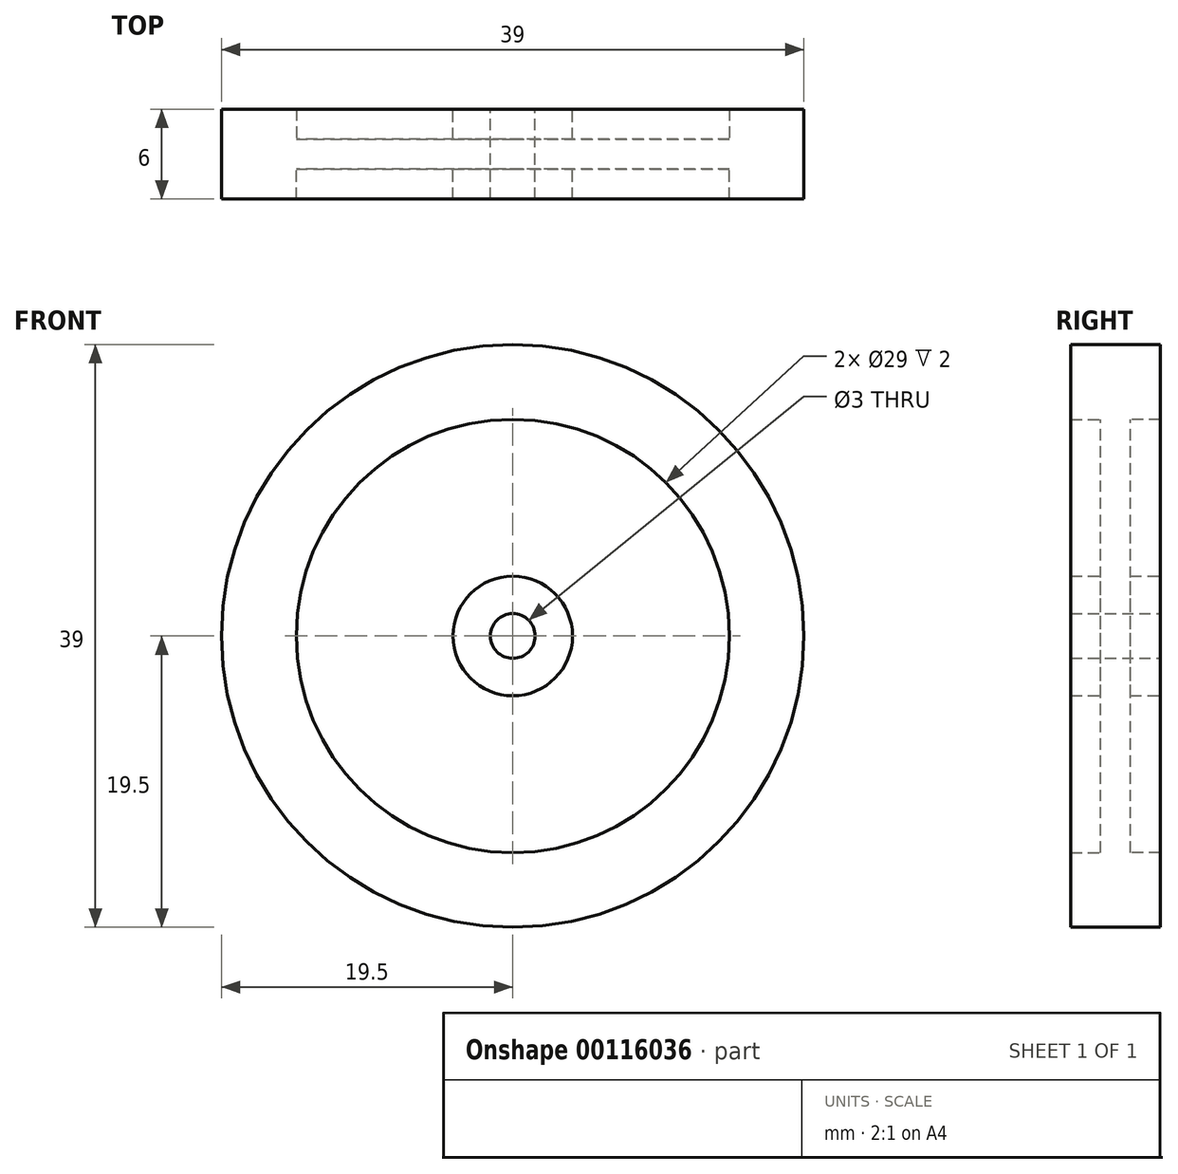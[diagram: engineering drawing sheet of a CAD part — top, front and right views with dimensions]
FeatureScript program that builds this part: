
annotation { "Feature Type Name" : "Feature", "Feature Type Description" : "" }
export const myFeature = defineFeature(function(context is Context, id is Id, definition is map)
    precondition{}
    {
        {
            var Q0;
            Q0=qCreatedBy(makeId("Front.planeOp"),FACE);
            var sketch = newSketch(context, id + "F0", { "sketchPlane" : qUnion([Q0])});
            skCircle(sketch, "E0", {"center": v(0, 0) * mm, "radius": 14.5 * mm});
            skCircle(sketch, "E1", {"center": v(0, 0) * mm, "radius": 4 * mm});
            skCircle(sketch, "E2", {"center": v(0, 0) * mm, "radius": 19.5 * mm});
            skCircle(sketch, "E3", {"center": v(0, 0) * mm, "radius": 1.5 * mm});
            skSolve(sketch);
        }
        {
            var Q0;
            Q0=makeQuery(id+"F0.imprint","IMPRINT",FACE,{"disambiguationData":[TD([[makeQuery(id+"F0.imprint","IMPRINT",EDGE,{"derivedFrom":sQuery(id+"F0.wireOp",EDGE,"E1")}),1.0]])]});
            extrude(context, id + "F1", {"entities" : qUnion([Q0]), "depth" : 3 * mm});
        }
        {
            var Q0;
            Q0=makeQuery(id+"F0.imprint","IMPRINT",FACE,{"disambiguationData":[TD([[makeQuery(id+"F0.imprint","IMPRINT",EDGE,{"derivedFrom":sQuery(id+"F0.wireOp",EDGE,"E1")}),1.0]])]});
            extrude(context, id + "F2", {"entities" : qUnion([Q0]), "operationType" : NewBodyOperationType.ADD, "oppositeDirection" : true, "depth" : 3 * mm});
        }
        {
            var Q0;
            Q0=makeQuery(id+"F0.imprint","IMPRINT",FACE,{"disambiguationData":[TD([[makeQuery(id+"F0.imprint","IMPRINT",EDGE,{"derivedFrom":sQuery(id+"F0.wireOp",EDGE,"E0")}),1.0]])]});
            extrude(context, id + "F3", {"entities" : qUnion([Q0]), "operationType" : NewBodyOperationType.ADD, "depth" : 1 * mm});
        }
        {
            var Q0;
            Q0=makeQuery(id+"F0.imprint","IMPRINT",FACE,{"disambiguationData":[TD([[makeQuery(id+"F0.imprint","IMPRINT",EDGE,{"derivedFrom":sQuery(id+"F0.wireOp",EDGE,"E0")}),1.0]])]});
            extrude(context, id + "F4", {"entities" : qUnion([Q0]), "operationType" : NewBodyOperationType.ADD, "oppositeDirection" : true, "depth" : 1 * mm});
        }
        {
            var Q0;
            Q0=makeQuery(id+"F0.imprint","IMPRINT",FACE,{"disambiguationData":[TD([[makeQuery(id+"F0.imprint","IMPRINT",EDGE,{"derivedFrom":sQuery(id+"F0.wireOp",EDGE,"E0")}),-1.0]])]});
            extrude(context, id + "F5", {"entities" : qUnion([Q0]), "operationType" : NewBodyOperationType.ADD, "depth" : 3 * mm});
        }
        {
            var Q0;
            Q0=makeQuery(id+"F0.imprint","IMPRINT",FACE,{"disambiguationData":[TD([[makeQuery(id+"F0.imprint","IMPRINT",EDGE,{"derivedFrom":sQuery(id+"F0.wireOp",EDGE,"E0")}),-1.0]])]});
            extrude(context, id + "F6", {"entities" : qUnion([Q0]), "operationType" : NewBodyOperationType.ADD, "oppositeDirection" : true, "depth" : 3 * mm});
        }
    });
